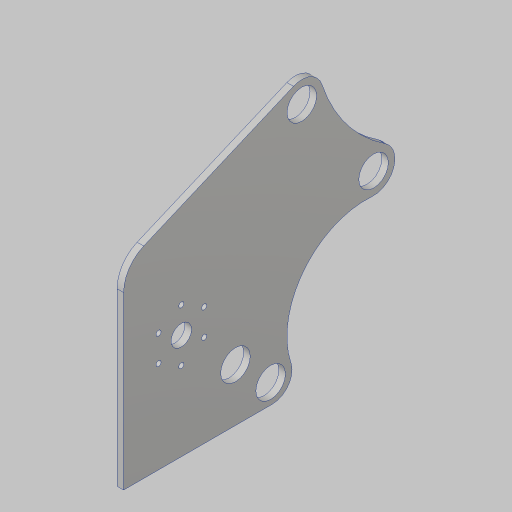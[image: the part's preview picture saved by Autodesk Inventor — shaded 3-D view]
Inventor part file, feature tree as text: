
AUTODESK INVENTOR PART (.ipt)
format: ipt  version: 2023.5 (Build 275446000, 446)  size: 195,072 bytes
history: native  units: in
note: dims shown in document units (in); Inventor stores cm internally (conversion verified against a paired STEP export)
features: sketch x3, extrude x2, projected_geometry x2, hole x1
ambient origin geometry x8: Origin, YZ Plane, XZ Plane, XY Plane, X Axis, Y Axis, Z Axis, Center Point
bodies: Solid1 (feature_tree)
feature tree (8):
  extrude  "Extrusion1"  Depth=3.0in
  sketch  "Sketch3"  dims[d4=0.5in d5=12.0in]
  sketch  "Sketch4"  dims[d6=4.5in d7=1.25in d8=2.0in d9=5.0in d10=6.0in d11=1.125in d12=1.25in d13=1.0in d14=1.8307in d15=1.75in d16=6.5in d17=3.0in d18=4.4882in d20=1.125in d21=1.125in d22=1.125in d23=0.25in d24=0.25in d25=0.25in d26=3.0in d27=7.0in d28=6.5in d29=6.0in d30=1.25in d33=0.25in d34=0.0in d35=0.75in d36=3.0in d37=5.0in d38=0.25in d39=0.0in d40=2.0in d41=0.75in d42=16.0in d43=5.0in d44=0.313in d45=0.313in d46=1.5748in d48=1.0in d49=0.3937in d51=1.0in d53=0.78in d54=2.8691in d55=4.0in d56=1.0in d57=0.0in d58=2.0in d59=2.3622in d61=360.0deg d63=0.201in d64=0.75in d65=0.385in d66=0.25in d67=0.5635in d68=1.0in d69=0.8108in d70=7.7362in]
  extrude  "Extrusion2"  Depth=12.0in
  hole  "Hole1"  [1 undecoded]
  sketch  "Sketch2"  dims[d2=5.0in d3=3.0in]
  projected_geometry  "Project Cut Edges1"
  projected_geometry  "Project Cut Edges2"
note: 1 required parameter value undecoded (feature->parameter linkage not recoverable at this tier; creation-order binding heuristic only, values carry confidence <= 0.55)
